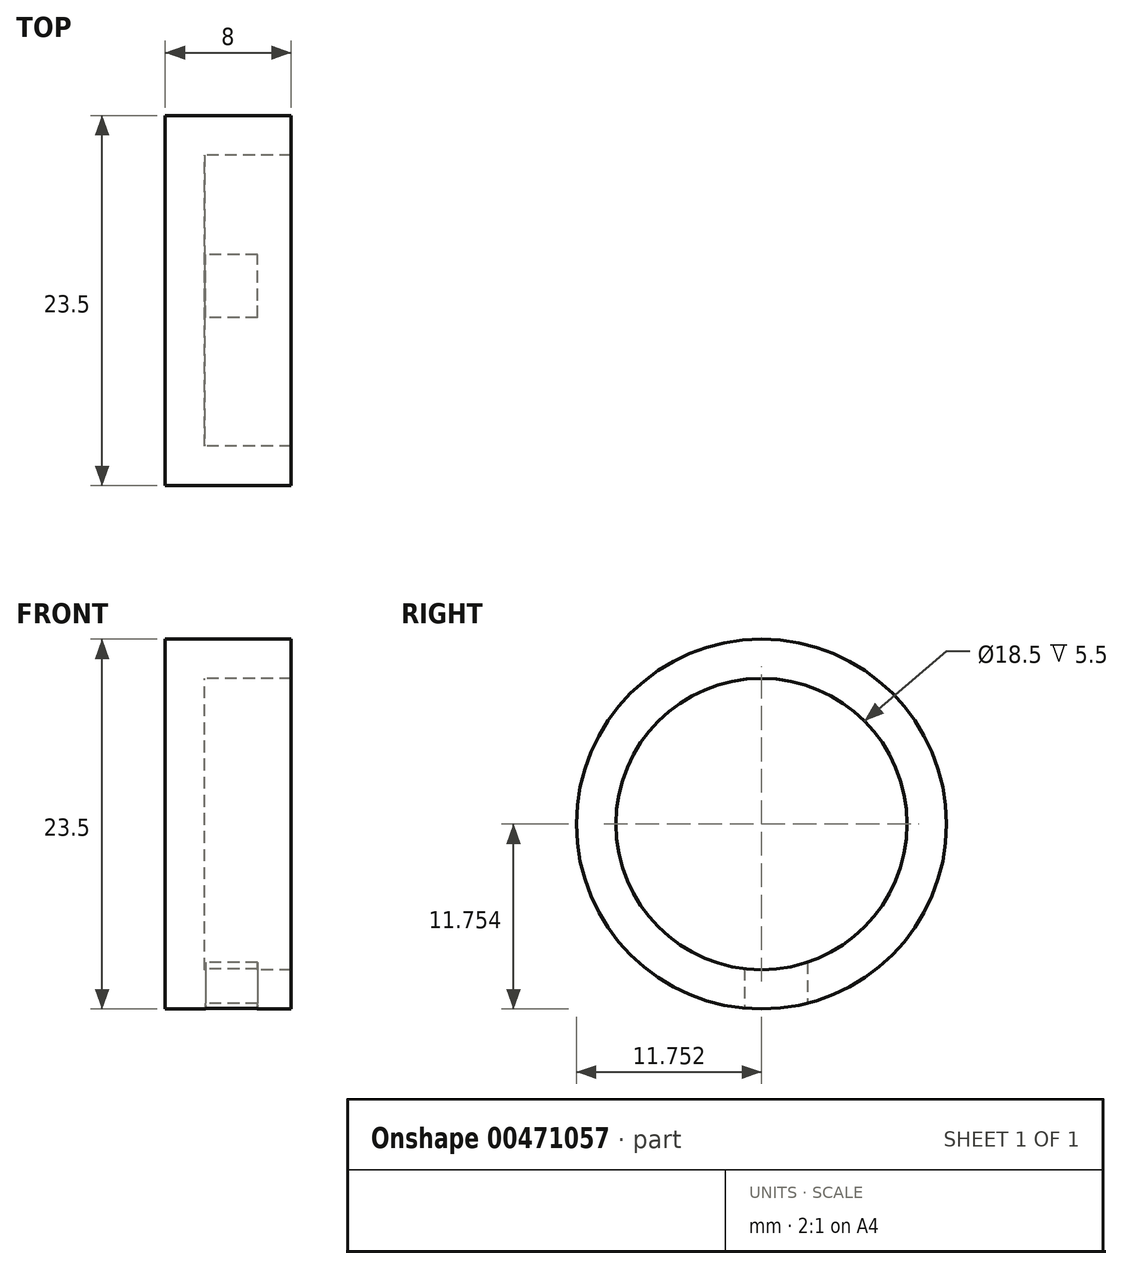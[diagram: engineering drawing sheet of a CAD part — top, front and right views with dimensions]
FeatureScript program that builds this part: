
annotation { "Feature Type Name" : "Feature", "Feature Type Description" : "" }
export const myFeature = defineFeature(function(context is Context, id is Id, definition is map)
    precondition{}
    {
        {
            var Q0;
            Q0=qCreatedBy(makeId("Right.planeOp"),FACE);
            var sketch = newSketch(context, id + "F0", { "sketchPlane" : qUnion([Q0])});
            skCircle(sketch, "E0", {"center": v(-7.94, 23.81) * mm, "radius": 11.75 * mm});
            skSolve(sketch);
        }
        {
            var Q0;
            Q0 = qSketchRegion(id + "F0", true);
            extrude(context, id + "F1", {"entities" : qUnion([Q0]), "depth" : 8 * mm, "offsetDistance" : 25 * mm});
        }
        {
            var Q0;
            Q0=makeQuery(id+"F1.opExtrude","CAP_FACE",FACE,{"disambiguationData":[OSD([sQuery(id+"F0.wireOp",EDGE,"E0")])],"isStart":false});
            shell(context, id + "F2", {"entities" : qUnion([Q0]), "thickness" : 2.5 * mm});
        }
        {
            var Q0;
            Q0=qCreatedBy(makeId("Top.planeOp"),FACE);
            var sketch = newSketch(context, id + "F3", { "sketchPlane" : qUnion([Q0])});
            skLineSegment(sketch, "E1.bottom", {"start": v(2.56, -5.01) * mm, "end": v(5.86, -5.01) * mm});
            skLineSegment(sketch, "E1.top", {"start": v(2.56, -9.01) * mm, "end": v(5.86, -9.01) * mm});
            skLineSegment(sketch, "E1.left", {"start": v(2.56, -5.01) * mm, "end": v(2.56, -9.01) * mm});
            skLineSegment(sketch, "E1.right", {"start": v(5.86, -5.01) * mm, "end": v(5.86, -9.01) * mm});
            skSolve(sketch);
        }
        {
            var Q0;
            Q0 = qSketchRegion(id + "F3", true);
            extrude(context, id + "F4", {"entities" : qUnion([Q0]), "operationType" : NewBodyOperationType.REMOVE, "depth" : 25 * mm, "offsetDistance" : 25 * mm});
        }
    });
